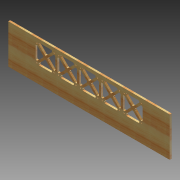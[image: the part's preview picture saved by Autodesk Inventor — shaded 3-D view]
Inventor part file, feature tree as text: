
AUTODESK INVENTOR PART (.ipt)
format: ipt  version: 2012 (Build 160160000, 160)  size: 297,472 bytes
history: native  units: in
note: dims shown in document units (in); Inventor stores cm internally (conversion verified against a paired STEP export)
features: extrude x1, fillet x1, sketch x1
ambient origin geometry x8: Origin, YZ Plane, XZ Plane, XY Plane, X Axis, Y Axis, Z Axis, Center Point
bodies: Solid1 (feature_tree)
feature tree (3):
  extrude  "Extrusion1"  Depth=9.0in
  fillet  "Fillet1"  Radius=0.4375in
  sketch  "Sketch1"  dims[d0=37.0in d1=9.0in d2=0.4375in d3=0.0in d4=6.0in d5=18.25in d6=5.0in d7=5.0in d9=0.25in d10=0.5in d18=3.937in d19=3.937in d20=0.25in d21=0.25in d22=0.25in d23=0.25in d24=1.5748in d26=360.0deg d28=1.9685in d30=5.0in d31=0.3937in d33=1.0in]
